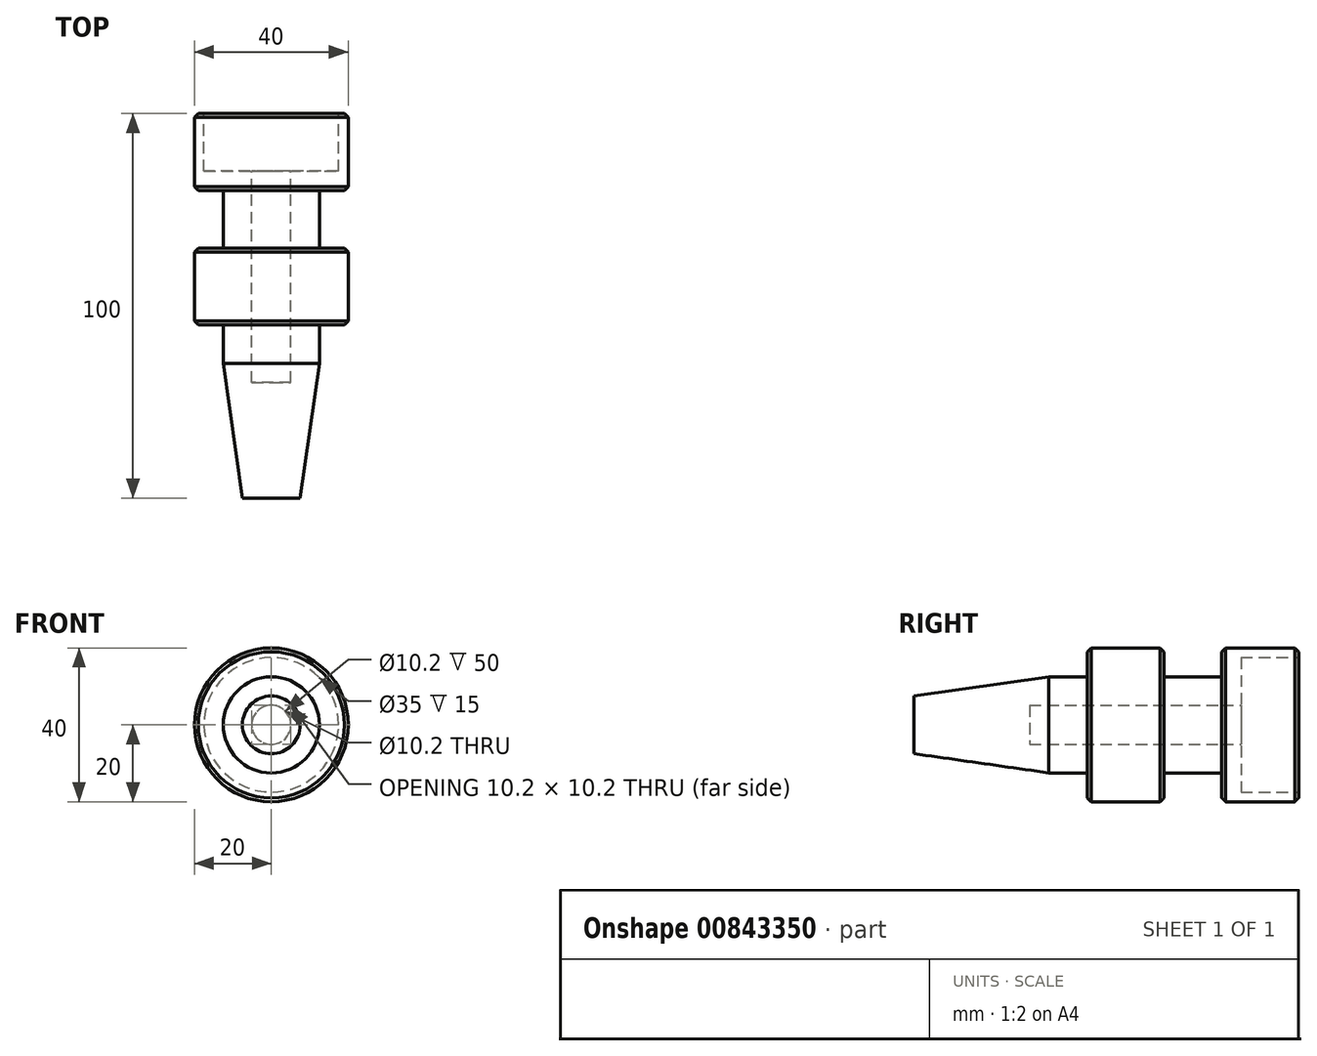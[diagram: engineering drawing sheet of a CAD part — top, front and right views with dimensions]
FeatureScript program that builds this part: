
annotation { "Feature Type Name" : "Feature", "Feature Type Description" : "" }
export const myFeature = defineFeature(function(context is Context, id is Id, definition is map)
    precondition{}
    {
        {
            var Q0;
            Q0=qCreatedBy(makeId("Front.planeOp"),FACE);
            var sketch = newSketch(context, id + "F0", { "sketchPlane" : qUnion([Q0])});
            skCircle(sketch, "E0", {"center": v(0, 0) * mm, "radius": 20 * mm});
            skSolve(sketch);
        }
        {
            var Q0;
            Q0=makeQuery(id+"F0.imprint","IMPRINT",FACE,{"disambiguationData":[TD([[makeQuery(id+"F0.imprint","IMPRINT",EDGE,{"derivedFrom":sQuery(id+"F0.wireOp",EDGE,"E0")}),1.0]])]});
            extrude(context, id + "F1", {"entities" : qUnion([Q0]), "depth" : 20 * mm, "offsetDistance" : 25 * mm});
        }
        {
            var Q0;
            Q0=makeQuery(id+"F1.opExtrude","CAP_FACE",FACE,{"disambiguationData":[OSD([sQuery(id+"F0.wireOp",EDGE,"E0")])],"isStart":false});
            var sketch = newSketch(context, id + "F2", { "sketchPlane" : qUnion([Q0])});
            skCircle(sketch, "E1", {"center": v(0, 0) * mm, "radius": 12.5 * mm});
            skSolve(sketch);
        }
        {
            var Q0;
            Q0=makeQuery(id+"F2.imprint","IMPRINT",FACE,{"disambiguationData":[TD([[makeQuery(id+"F2.imprint","IMPRINT",EDGE,{"derivedFrom":sQuery(id+"F2.wireOp",EDGE,"E1")}),1.0]])]});
            var Q1;
            Q1=sQuery(id+"F2.wireOp",EDGE,"E1");
            extrude(context, id + "F3", {"entities" : qUnion([Q0]), "surfaceEntities" : qUnion([Q1]), "depth" : 15 * mm, "offsetDistance" : 25 * mm});
        }
        {
            var Q0;
            Q0=makeQuery(id+"F3.opExtrude","CAP_FACE",FACE,{"disambiguationData":[OSD([sQuery(id+"F2.wireOp",EDGE,"E1")])],"isStart":false});
            var sketch = newSketch(context, id + "F4", { "sketchPlane" : qUnion([Q0])});
            skCircle(sketch, "E2", {"center": v(0, 0) * mm, "radius": 20 * mm});
            skSolve(sketch);
        }
        {
            var Q0;
            Q0=makeQuery(id+"F4.imprint","IMPRINT",FACE,{"disambiguationData":[TD([[makeQuery(id+"F4.imprint","IMPRINT",EDGE,{"derivedFrom":sQuery(id+"F4.wireOp",EDGE,"E2")}),1.0]])]});
            var Q1;
            Q1=makeQuery(id+"F4.imprint","IMPRINT",FACE,{"disambiguationData":[TD([[makeQuery(id+"F4.imprint","IMPRINT",EDGE,{"derivedFrom":makeQuery(id+"F3.opExtrude","CAP_EDGE",EDGE,{"disambiguationData":[OSD([sQuery(id+"F2.wireOp",EDGE,"E1")])],"isStart":false})}),1.0]])]});
            extrude(context, id + "F5", {"entities" : qUnion([Q0, Q1]), "operationType" : NewBodyOperationType.ADD, "depth" : 20 * mm, "offsetDistance" : 25 * mm});
        }
        {
            var Q0;
            Q0=makeQuery(id+"F5.opExtrude","CAP_FACE",FACE,{"disambiguationData":[OSD([sQuery(id+"F4.wireOp",EDGE,"E2")])],"isStart":false});
            var sketch = newSketch(context, id + "F6", { "sketchPlane" : qUnion([Q0])});
            skCircle(sketch, "E3", {"center": v(0, 0) * mm, "radius": 12.5 * mm});
            skSolve(sketch);
        }
        {
            var Q0;
            Q0=makeQuery(id+"F6.imprint","IMPRINT",FACE,{"disambiguationData":[TD([[makeQuery(id+"F6.imprint","IMPRINT",EDGE,{"derivedFrom":sQuery(id+"F6.wireOp",EDGE,"E3")}),1.0]])]});
            extrude(context, id + "F7", {"entities" : qUnion([Q0]), "operationType" : NewBodyOperationType.ADD, "depth" : 10 * mm, "offsetDistance" : 25 * mm});
        }
        {
            var Q0;
            Q0=makeQuery(id+"F7.opExtrude","CAP_FACE",FACE,{"disambiguationData":[OSD([sQuery(id+"F6.wireOp",EDGE,"E3")])],"isStart":false});
            var sketch = newSketch(context, id + "F8", { "sketchPlane" : qUnion([Q0])});
            skCircle(sketch, "E4", {"center": v(0, 0) * mm, "radius": 12.5 * mm});
            skSolve(sketch);
        }
        {
            var Q0;
            Q0=makeQuery(id+"F8.imprint","IMPRINT",FACE,{"disambiguationData":[TD([[makeQuery(id+"F8.imprint","IMPRINT",EDGE,{"derivedFrom":sQuery(id+"F8.wireOp",EDGE,"E4")}),1.0]])]});
            cPlane(context, id + "F9", {"entities" : qUnion([Q0]), "cplaneType" : CPlaneType.OFFSET, "offset" : 35 * mm, "width" : 150 * mm, "height" : 150 * mm});
        }
        {
            var Q0;
            Q0=qCreatedBy(id+"F9.planeOp",FACE);
            var sketch = newSketch(context, id + "F10", { "sketchPlane" : qUnion([Q0])});
            skCircle(sketch, "E5", {"center": v(0, 0) * mm, "radius": 7.5 * mm});
            skSolve(sketch);
        }
        {
            var Q1;
            Q1=makeQuery(id+"F8.imprint","IMPRINT",FACE,{"disambiguationData":[TD([[makeQuery(id+"F8.imprint","IMPRINT",EDGE,{"derivedFrom":sQuery(id+"F8.wireOp",EDGE,"E4")}),1.0]])]});
            var Q2;
            Q2=makeQuery(id+"F10.imprint","IMPRINT",FACE,{"disambiguationData":[TD([[makeQuery(id+"F10.imprint","IMPRINT",EDGE,{"derivedFrom":sQuery(id+"F10.wireOp",EDGE,"E5")}),1.0]])]});
            loft(context, id + "F11", {"operationType" : NewBodyOperationType.ADD, "sheetProfilesArray" : [{ "sheetProfileEntities" : qUnion([Q1]) }, { "sheetProfileEntities" : qUnion([Q2]) }]});
        }
        {
            var Q0;
            Q0=makeQuery(id+"F1.opExtrude","CAP_EDGE",EDGE,{"disambiguationData":[OSD([sQuery(id+"F0.wireOp",EDGE,"E0")])],"isStart":true});
            var Q1;
            Q1=makeQuery(id+"F1.opExtrude","CAP_EDGE",EDGE,{"disambiguationData":[OSD([sQuery(id+"F0.wireOp",EDGE,"E0")])],"isStart":false});
            var Q2;
            Q2=makeQuery(id+"F5.opExtrude","CAP_EDGE",EDGE,{"disambiguationData":[OSD([sQuery(id+"F4.wireOp",EDGE,"E2")])],"isStart":true});
            var Q3;
            Q3=makeQuery(id+"F5.opExtrude","CAP_EDGE",EDGE,{"disambiguationData":[OSD([sQuery(id+"F4.wireOp",EDGE,"E2")])],"isStart":false});
            chamfer(context, id + "F12", {"entities" : qUnion([Q0, Q1, Q2, Q3]), "width" : 1 * mm, "tangentPropagation" : true});
        }
        {
            var Q0;
            Q0=makeQuery(id+"F1.opExtrude","CAP_FACE",FACE,{"disambiguationData":[OSD([sQuery(id+"F0.wireOp",EDGE,"E0")])],"isStart":true});
            var sketch = newSketch(context, id + "F13", { "sketchPlane" : qUnion([Q0])});
            skCircle(sketch, "E6", {"center": v(0, 0) * mm, "radius": 17.5 * mm});
            skSolve(sketch);
        }
        {
            var Q0;
            Q0=makeQuery(id+"F13.imprint","IMPRINT",FACE,{"disambiguationData":[TD([[makeQuery(id+"F13.imprint","IMPRINT",EDGE,{"derivedFrom":sQuery(id+"F13.wireOp",EDGE,"E6")}),1.0]])]});
            extrude(context, id + "F14", {"entities" : qUnion([Q0]), "operationType" : NewBodyOperationType.REMOVE, "oppositeDirection" : true, "depth" : 15 * mm, "offsetDistance" : 25 * mm});
        }
        {
            var Q0;
            Q0=makeQuery(id+"F14.boolean.opBoolean","COPY",FACE,{"derivedFrom":makeQuery(id+"F14.opExtrude","CAP_FACE",FACE,{"disambiguationData":[OSD([sQuery(id+"F13.wireOp",EDGE,"E6")])],"isStart":false})});
            var sketch = newSketch(context, id + "F15", { "sketchPlane" : qUnion([Q0])});
            skCircle(sketch, "E7", {"center": v(0, 0) * mm, "radius": 5.1 * mm});
            skSolve(sketch);
        }
        {
            var Q0;
            Q0=makeQuery(id+"F15.imprint","IMPRINT",FACE,{"disambiguationData":[TD([[makeQuery(id+"F15.imprint","IMPRINT",EDGE,{"derivedFrom":sQuery(id+"F15.wireOp",EDGE,"E7")}),1.0]])]});
            extrude(context, id + "F16", {"entities" : qUnion([Q0]), "operationType" : NewBodyOperationType.REMOVE, "oppositeDirection" : true, "depth" : 55 * mm, "offsetDistance" : 25 * mm});
        }
    });
